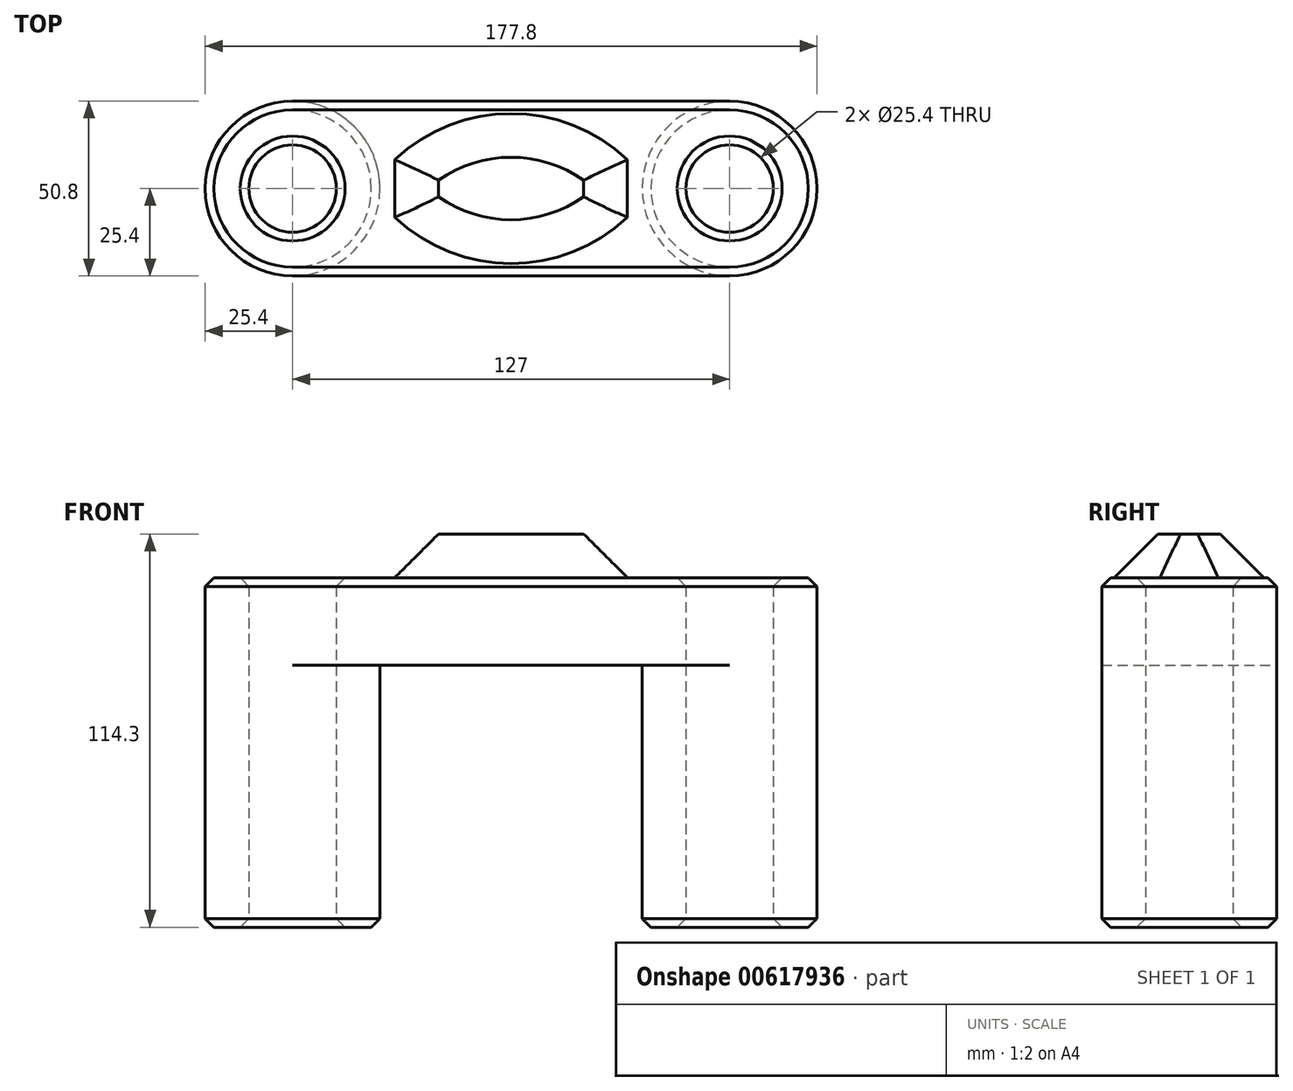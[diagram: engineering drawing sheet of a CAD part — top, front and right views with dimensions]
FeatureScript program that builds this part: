
annotation { "Feature Type Name" : "Feature", "Feature Type Description" : "" }
export const myFeature = defineFeature(function(context is Context, id is Id, definition is map)
    precondition{}
    {
        {
            var Q0;
            Q0=qCreatedBy(makeId("Top.planeOp"),FACE);
            var sketch = newSketch(context, id + "F0", { "sketchPlane" : qUnion([Q0])});
            skCircle(sketch, "E0", {"center": v(0, 0) * mm, "radius": 25.4 * mm});
            skCircle(sketch, "E1", {"center": v(127, 0) * mm, "radius": 25.4 * mm});
            skLineSegment(sketch, "E2", {"start": v(0, -25.4) * mm, "end": v(127, -25.4) * mm});
            skLineSegment(sketch, "E3", {"start": v(127, 25.4) * mm, "end": v(0, 25.4) * mm});
            skCircle(sketch, "E4", {"center": v(127, 0) * mm, "radius": 12.7 * mm});
            skCircle(sketch, "E5", {"center": v(0, 0) * mm, "radius": 12.7 * mm});
            skSolve(sketch);
        }
        {
            var Q0;
            Q0 = qSketchRegion(id + "F0", true);
            extrude(context, id + "F1", {"entities" : qUnion([Q0]), "depth" : 25.4 * mm, "offsetDistance" : 25.4 * mm});
        }
        {
            var Q0;
            Q0=makeQuery(id+"F0.imprint","IMPRINT",FACE,{"disambiguationData":[TD([[makeQuery(id+"F0.imprint","IMPRINT",EDGE,{"derivedFrom":sQuery(id+"F0.wireOp",EDGE,"E5")}),-1.0]])]});
            var Q1;
            Q1=makeQuery(id+"F0.imprint","IMPRINT",FACE,{"disambiguationData":[TD([[makeQuery(id+"F0.imprint","IMPRINT",EDGE,{"derivedFrom":sQuery(id+"F0.wireOp",EDGE,"E4")}),-1.0]])]});
            extrude(context, id + "F2", {"entities" : qUnion([Q0, Q1]), "operationType" : NewBodyOperationType.ADD, "oppositeDirection" : true, "depth" : 76.2 * mm, "offsetDistance" : 25.4 * mm});
        }
        {
            var Q0;
            Q0=makeQuery(id+"F1.opExtrude","CAP_FACE",FACE,{"disambiguationData":[OSD([sQuery(id+"F0.wireOp",EDGE,"E0"),sQuery(id+"F0.wireOp",EDGE,"E1"),sQuery(id+"F0.wireOp",EDGE,"E2"),sQuery(id+"F0.wireOp",EDGE,"E3"),sQuery(id+"F0.wireOp",EDGE,"E4"),sQuery(id+"F0.wireOp",EDGE,"E5")])],"isStart":false});
            var sketch = newSketch(context, id + "F3", { "sketchPlane" : qUnion([Q0])});
            skSolve(sketch);
        }
        {
            var Q0;
            Q0=makeQuery(id+"F3.imprint","IMPRINT",FACE,{"disambiguationData":[TD([[makeQuery(id+"F3.imprint","IMPRINT",EDGE,{"derivedFrom":makeQuery(id+"F1.opExtrude","CAP_EDGE",EDGE,{"disambiguationData":[OSD([sQuery(id+"F0.wireOp",EDGE,"E0")])],"isStart":false})}),1.0]])]});
            var sketch = newSketch(context, id + "F4", { "sketchPlane" : qUnion([Q0])});
            skLineSegment(sketch, "E6.left", {"start": v(97.3, -8.39) * mm, "end": v(97.3, 8.39) * mm});
            skLineSegment(sketch, "E6.right", {"start": v(29.7, -8.39) * mm, "end": v(29.7, 8.39) * mm});
            skPoint(sketch, "E6.middle", {"position": v(63.5, 0) * mm});
            skArc(sketch, "E7", {"start": v(97.3, 8.39) * mm, "mid": v(63.5, 21.78) * mm, "end": v(29.7, 8.39) * mm});
            skArc(sketch, "E8.MirrorCS", {"start": v(97.3, -8.39) * mm, "mid": v(63.5, -21.78) * mm, "end": v(29.7, -8.39) * mm});
            skSolve(sketch);
        }
        {
            var Q0;
            Q0 = qSketchRegion(id + "F4", true);
            extrude(context, id + "F5", {"entities" : qUnion([Q0]), "operationType" : NewBodyOperationType.ADD, "depth" : 12.7 * mm, "offsetDistance" : 25.4 * mm});
        }
        {
            var Q0;
            Q0=makeQuery(id+"F5.opExtrude","CAP_EDGE",EDGE,{"disambiguationData":[OSD([sQuery(id+"F4.wireOp",EDGE,"E8.MirrorCS")])],"isStart":false});
            var Q1;
            Q1=makeQuery(id+"F5.opExtrude","CAP_EDGE",EDGE,{"disambiguationData":[OSD([sQuery(id+"F4.wireOp",EDGE,"E6.left")])],"isStart":false});
            var Q2;
            Q2=makeQuery(id+"F5.opExtrude","CAP_EDGE",EDGE,{"disambiguationData":[OSD([sQuery(id+"F4.wireOp",EDGE,"E7")])],"isStart":false});
            var Q3;
            Q3=makeQuery(id+"F5.opExtrude","CAP_EDGE",EDGE,{"disambiguationData":[OSD([sQuery(id+"F4.wireOp",EDGE,"E6.right")])],"isStart":false});
            chamfer(context, id + "F6", {"entities" : qUnion([Q0, Q1, Q2, Q3]), "width" : 12.7 * mm, "tangentPropagation" : true});
        }
        {
            var Q0;
            Q0=makeQuery(id+"F1.opExtrude","CAP_EDGE",EDGE,{"disambiguationData":[OSD([sQuery(id+"F0.wireOp",EDGE,"E4")])],"isStart":false});
            var Q1;
            Q1=makeQuery(id+"F1.opExtrude","CAP_EDGE",EDGE,{"disambiguationData":[OSD([sQuery(id+"F0.wireOp",EDGE,"E5")])],"isStart":false});
            chamfer(context, id + "F7", {"entities" : qUnion([Q0, Q1]), "width" : 2.54 * mm, "tangentPropagation" : true});
        }
        {
            var Q0;
            Q0=makeQuery(id+"F2.opExtrude","CAP_EDGE",EDGE,{"disambiguationData":[OSD([sQuery(id+"F0.wireOp",EDGE,"E4")])],"isStart":false});
            var Q1;
            Q1=makeQuery(id+"F2.opExtrude","CAP_EDGE",EDGE,{"disambiguationData":[OSD([sQuery(id+"F0.wireOp",EDGE,"E1")])],"isStart":false});
            var Q2;
            Q2=makeQuery(id+"F2.opExtrude","CAP_EDGE",EDGE,{"disambiguationData":[OSD([sQuery(id+"F0.wireOp",EDGE,"E0")])],"isStart":false});
            var Q3;
            Q3=makeQuery(id+"F2.opExtrude","CAP_EDGE",EDGE,{"disambiguationData":[OSD([sQuery(id+"F0.wireOp",EDGE,"E5")])],"isStart":false});
            chamfer(context, id + "F8", {"entities" : qUnion([Q0, Q1, Q2, Q3]), "width" : 2.54 * mm, "tangentPropagation" : true});
        }
        {
            var Q0;
            Q0=makeQuery(id+"F1.opExtrude","CAP_EDGE",EDGE,{"disambiguationData":[OSD([sQuery(id+"F0.wireOp",EDGE,"E2")])],"isStart":false});
            chamfer(context, id + "F9", {"entities" : qUnion([Q0]), "width" : 2.54 * mm, "tangentPropagation" : true});
        }
    });
